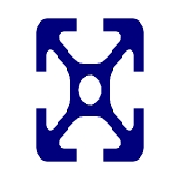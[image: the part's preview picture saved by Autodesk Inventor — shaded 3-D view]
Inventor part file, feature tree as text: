
AUTODESK INVENTOR PART (.ipt)
format: ipt  version: 2020 (Build 240168000, 168)  size: 272,384 bytes
history: native  units: mm
features: other x16, sketch x8, plane x1, split x1
ambient origin geometry x8: Origin, YZ Plane, XZ Plane, XY Plane, X Axis, Y Axis, Z Axis, Center Point
bodies: Body (feature_tree)
feature tree (26):
  other  "Řízená délka"
  other  "Těleso1"
  other  "Start Plane"
  other  "End Plane"
  other  "iFeatureSketch"
  other  "DRAZKA_20:1"
  other  "DRAZKA_20:2"
  other  "DRAZKA_20:3"
  other  "DRAZKA_20:4"
  other  "DIRA_20:1"
  other  "DRAZKA_20:1Axis"
  other  "DRAZKA_20:2Axis"
  other  "DRAZKA_20:3Axis"
  other  "DRAZKA_20:4Axis"
  other  "DIRA_20:1Axis"
  plane  "Work Plane5"
  split  "Split1"
  sketch  "Sketch"  dims[d2=20.0mm d3=20.0mm d4=2.0mm d9=-0.0mm d10=90.0mm d11=0.13mm d12=0.0mm d15=0.83mm d16=0.83mm d17=9.8mm d18=3.0mm d19=4.55mm d20=45.0deg d21=5.2mm d22=1.8mm d24=1.0mm d26=0.83mm d27=0.83mm d28=9.8mm d29=3.0mm d30=4.55mm d31=45.0deg d32=5.2mm d33=1.8mm d35=1.0mm d37=0.83mm d38=0.83mm d39=9.8mm d40=3.0mm d41=4.55mm d42=45.0deg d43=5.2mm d44=1.8mm d46=1.0mm d48=0.83mm d49=0.83mm d50=9.8mm d51=3.0mm d52=4.55mm d53=45.0deg d54=5.2mm d55=1.8mm d57=1.0mm d59=4.3mm d60=0.0mm d61=0.0mm d62=0.0mm d63=0.0mm d64=0.0mm d65=0.0mm d66=0.0mm d67=0.0mm d76=90.0deg d14=90.0mm]
  sketch  "Náčrt11"
  other  "Pracovní rovina4"
  sketch  "Náčrt12"
  sketch  "Náčrt6"
  sketch  "Náčrt7"
  sketch  "Náčrt8"
  sketch  "Náčrt9"
  sketch  "Náčrt10"
